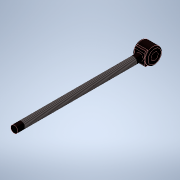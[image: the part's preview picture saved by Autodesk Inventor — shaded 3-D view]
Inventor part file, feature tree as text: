
AUTODESK INVENTOR PART (.ipt)
format: ipt  version: 2021 (Build 250183000, 183)  size: 145,408 bytes
history: native  units: mm
features: extrude x4, sketch x4, fillet x2, thread x1, plane x1
ambient origin geometry x8: Origin, YZ Plane, XZ Plane, XY Plane, X Axis, Y Axis, Z Axis, Center Point
bodies: Solid1 (feature_tree)
feature tree (12):
  extrude  "Extrusion1"  Depth=180.0mm TaperAngle=0.0deg
  thread  "Thread1"  [1 undecoded]
  extrude  "Extrusion2"  Depth=10.0mm
  extrude  "Extrusion3"  Depth=2.0mm
  fillet  "Fillet1"  Radius=5.0mm
  plane  "Work Plane1"
  extrude  "Extrusion4"  [1 undecoded]
  fillet  "Fillet2"  [1 undecoded]
  sketch  "Sketch1"  dims[d0=10.0mm d1=180.0mm d2=0.0mm d3=160.0mm d4=10.0mm]
  sketch  "Sketch2"  dims[d5=20.0mm d6=0.0mm d7=10.0mm]
  sketch  "Sketch3"  dims[d8=20.0mm d9=0.0mm d10=2.0mm d11=5.0mm d12=0.0mm]
  sketch  "Sketch4"  dims[d13=2.0mm]
note: 3 required parameter values undecoded (feature->parameter linkage not recoverable at this tier; creation-order binding heuristic only, values carry confidence <= 0.55)
